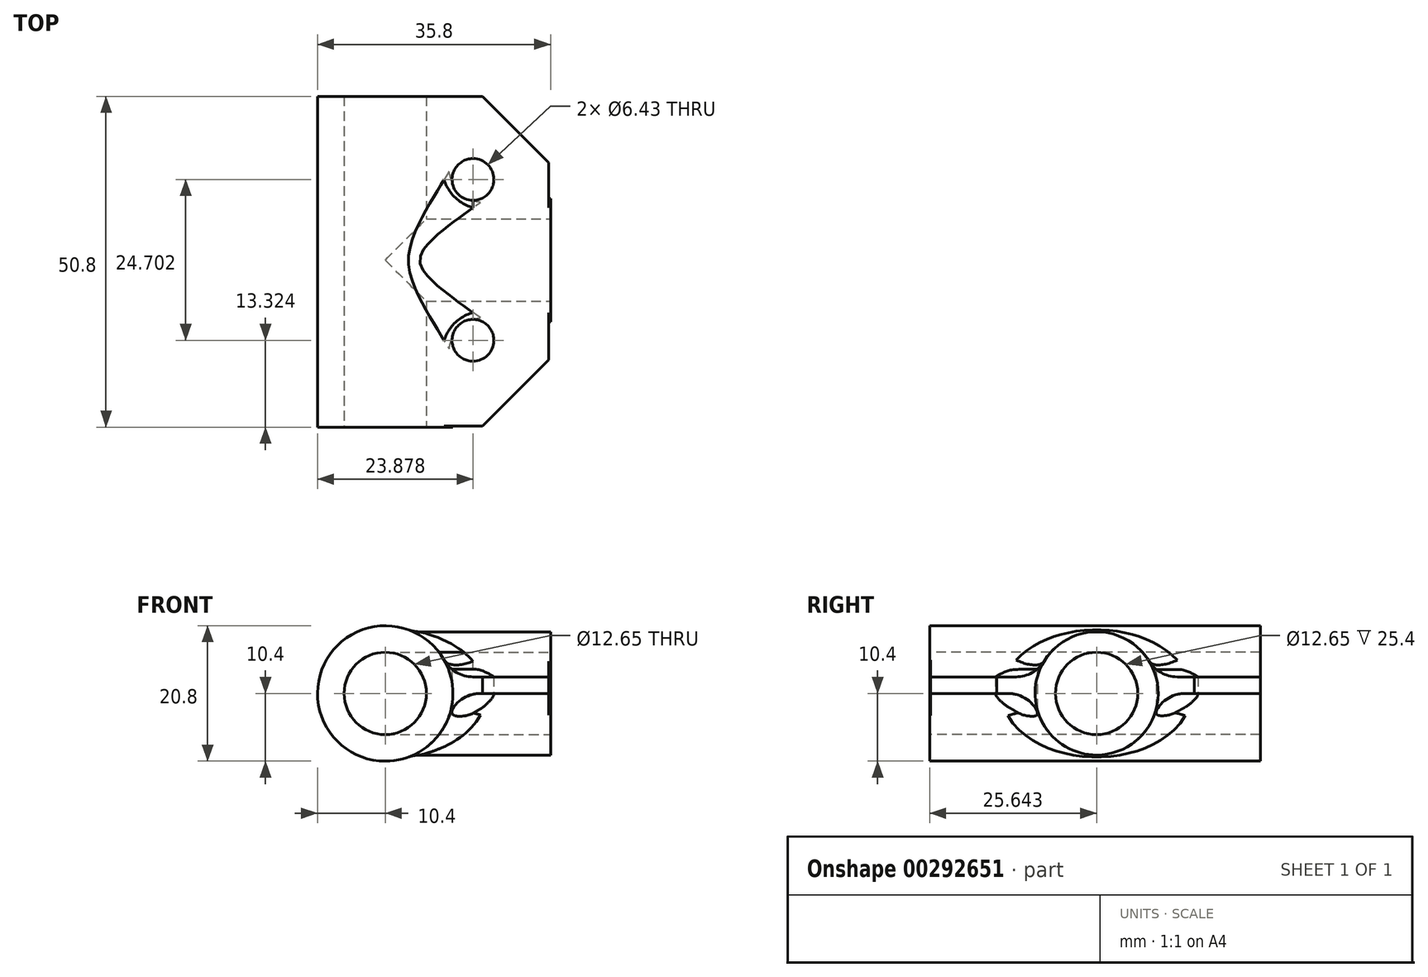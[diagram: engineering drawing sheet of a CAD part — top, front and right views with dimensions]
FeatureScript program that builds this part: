
annotation { "Feature Type Name" : "Feature", "Feature Type Description" : "" }
export const myFeature = defineFeature(function(context is Context, id is Id, definition is map)
    precondition{}
    {
        {
            var Q0;
            Q0=qCreatedBy(makeId("Front.planeOp"),FACE);
            var sketch = newSketch(context, id + "F0", { "sketchPlane" : qUnion([Q0])});
            skCircle(sketch, "E0", {"center": v(0, 0) * mm, "radius": 10.4 * mm});
            skSolve(sketch);
        }
        {
            var Q0;
            Q0=qCreatedBy(makeId("Top.planeOp"),FACE);
            var sketch = newSketch(context, id + "F1", { "sketchPlane" : qUnion([Q0])});
            skLineSegment(sketch, "E1.bottom", {"start": v(0, 0) * mm, "end": v(25.12, 0) * mm});
            skLineSegment(sketch, "E1.top", {"start": v(0, -50.67) * mm, "end": v(25.12, -50.67) * mm});
            skLineSegment(sketch, "E1.left", {"start": v(0, 0) * mm, "end": v(0, -50.67) * mm});
            skLineSegment(sketch, "E1.right", {"start": v(25.12, 0) * mm, "end": v(25.12, -50.67) * mm});
            skSolve(sketch);
        }
        {
            var Q0;
            Q0 = qSketchRegion(id + "F1", true);
            extrude(context, id + "F2", {"entities" : qUnion([Q0]), "depth" : 2.54 * mm});
        }
        {
            var Q0;
            Q0=makeQuery(id+"F0.imprint","IMPRINT",FACE,{"disambiguationData":[TD([[makeQuery(id+"F0.imprint","IMPRINT",EDGE,{"derivedFrom":sQuery(id+"F0.wireOp",EDGE,"E0")}),1.0]])]});
            var Q1;
            Q1=sQuery(id+"F0.wireOp",EDGE,"E0");
            extrude(context, id + "F3", {"entities" : qUnion([Q0]), "operationType" : NewBodyOperationType.ADD, "surfaceEntities" : qUnion([Q1]), "depth" : 50.8 * mm});
        }
        {
            var Q0;
            Q0=qCreatedBy(makeId("Right.planeOp"),FACE);
            var sketch = newSketch(context, id + "F4", { "sketchPlane" : qUnion([Q0])});
            skCircle(sketch, "E2", {"center": v(-25.16, 0) * mm, "radius": 9.46 * mm});
            skSolve(sketch);
        }
        {
            var Q0;
            Q0 = qSketchRegion(id + "F4", true);
            extrude(context, id + "F5", {"entities" : qUnion([Q0]), "operationType" : NewBodyOperationType.ADD, "depth" : 25.4 * mm});
        }
        {
            var Q0;
            {var subQ0=sQuery(id+"F1.wireOp",EDGE,"E1.top");var subQ1=makeQuery(id+"F2.opExtrude","CAP_FACE",FACE,{"disambiguationData":[OSD([sQuery(id+"F1.wireOp",EDGE,"E1.bottom"),subQ0,sQuery(id+"F1.wireOp",EDGE,"E1.left"),sQuery(id+"F1.wireOp",EDGE,"E1.right")])],"isStart":false});var subQ2=makeQuery(id+"F3.opExtrude","SWEPT_FACE",FACE,{"disambiguationData":[OSD([sQuery(id+"F0.wireOp",EDGE,"E0")])]});Q0=makeQuery(id+"F5.boolean.opBoolean","SPLIT",EDGE,{"disambiguationData":[TD([makeQuery(id+"F2.opExtrude","SWEPT_FACE",FACE,{"disambiguationData":[OSD([subQ0])]})])],"derivedFrom":makeQuery(id+"F3.boolean.opBoolean","INTERSECT",EDGE,{"derivedFrom":[subQ1,subQ2]})});}
            var Q1;
            Q1=makeQuery(id+"F5.boolean.opBoolean","INTERSECT",EDGE,{"disambiguationData":[OD(1.0)],"derivedFrom":[makeQuery(id+"F2.opExtrude","CAP_FACE",FACE,{"disambiguationData":[OSD([sQuery(id+"F1.wireOp",EDGE,"E1.bottom"),sQuery(id+"F1.wireOp",EDGE,"E1.top"),sQuery(id+"F1.wireOp",EDGE,"E1.left"),sQuery(id+"F1.wireOp",EDGE,"E1.right")])],"isStart":false}),makeQuery(id+"F5.opExtrude","SWEPT_FACE",FACE,{"disambiguationData":[OSD([sQuery(id+"F4.wireOp",EDGE,"E2")])]})]});
            fillet(context, id + "F6", {"entities" : qUnion([Q0, Q1]), "radius" : 5.08 * mm, "tangentPropagation" : true, "allowEdgeOverflow" : false});
        }
        {
            var Q0;
            Q0=makeQuery(id+"F5.boolean.opBoolean","INTERSECT",EDGE,{"disambiguationData":[OD(0.0)],"derivedFrom":[makeQuery(id+"F2.opExtrude","CAP_FACE",FACE,{"disambiguationData":[OSD([sQuery(id+"F1.wireOp",EDGE,"E1.bottom"),sQuery(id+"F1.wireOp",EDGE,"E1.top"),sQuery(id+"F1.wireOp",EDGE,"E1.left"),sQuery(id+"F1.wireOp",EDGE,"E1.right")])],"isStart":false}),makeQuery(id+"F5.opExtrude","SWEPT_FACE",FACE,{"disambiguationData":[OSD([sQuery(id+"F4.wireOp",EDGE,"E2")])]})]});
            fillet(context, id + "F7", {"entities" : qUnion([Q0]), "radius" : 5.08 * mm, "tangentPropagation" : true, "allowEdgeOverflow" : false});
        }
        {
            var Q0;
            {var subQ0=sQuery(id+"F0.wireOp",EDGE,"E0");var subQ1=makeQuery(id+"F3.opExtrude","SWEPT_FACE",FACE,{"disambiguationData":[OSD([subQ0])]});var subQ2=sQuery(id+"F1.wireOp",EDGE,"E1.bottom");var subQ3=makeQuery(id+"F2.opExtrude","CAP_FACE",FACE,{"disambiguationData":[OSD([subQ2,sQuery(id+"F1.wireOp",EDGE,"E1.top"),sQuery(id+"F1.wireOp",EDGE,"E1.left"),sQuery(id+"F1.wireOp",EDGE,"E1.right")])],"isStart":false});Q0=makeQuery(id+"F5.boolean.opBoolean","SPLIT",EDGE,{"disambiguationData":[TD([makeQuery(id+"F2.opExtrude","SWEPT_FACE",FACE,{"disambiguationData":[OSD([subQ2])]})])],"derivedFrom":makeQuery(id+"F3.boolean.opBoolean","INTERSECT",EDGE,{"derivedFrom":[subQ3,subQ1]})});}
            fillet(context, id + "F8", {"entities" : qUnion([Q0]), "radius" : 5.08 * mm, "tangentPropagation" : true, "allowEdgeOverflow" : false});
        }
        {
            var Q0;
            {var subQ0=sQuery(id+"F0.wireOp",EDGE,"E0");var subQ1=makeQuery(id+"F3.opExtrude","SWEPT_FACE",FACE,{"disambiguationData":[OSD([subQ0])]});var subQ2=sQuery(id+"F1.wireOp",EDGE,"E1.bottom");var subQ3=makeQuery(id+"F2.opExtrude","CAP_FACE",FACE,{"disambiguationData":[OSD([subQ2,sQuery(id+"F1.wireOp",EDGE,"E1.top"),sQuery(id+"F1.wireOp",EDGE,"E1.left"),sQuery(id+"F1.wireOp",EDGE,"E1.right")])],"isStart":true});Q0=makeQuery(id+"F5.boolean.opBoolean","SPLIT",EDGE,{"disambiguationData":[TD([makeQuery(id+"F2.opExtrude","SWEPT_FACE",FACE,{"disambiguationData":[OSD([subQ2])]})])],"derivedFrom":makeQuery(id+"F3.boolean.opBoolean","INTERSECT",EDGE,{"derivedFrom":[subQ3,subQ1]})});}
            var Q1;
            Q1=makeQuery(id+"F5.boolean.opBoolean","INTERSECT",EDGE,{"disambiguationData":[OD(0.0)],"derivedFrom":[makeQuery(id+"F2.opExtrude","CAP_FACE",FACE,{"disambiguationData":[OSD([sQuery(id+"F1.wireOp",EDGE,"E1.bottom"),sQuery(id+"F1.wireOp",EDGE,"E1.top"),sQuery(id+"F1.wireOp",EDGE,"E1.left"),sQuery(id+"F1.wireOp",EDGE,"E1.right")])],"isStart":true}),makeQuery(id+"F5.opExtrude","SWEPT_FACE",FACE,{"disambiguationData":[OSD([sQuery(id+"F4.wireOp",EDGE,"E2")])]})]});
            fillet(context, id + "F9", {"entities" : qUnion([Q0, Q1]), "radius" : 5.08 * mm, "tangentPropagation" : true, "allowEdgeOverflow" : false});
        }
        {
            var Q0;
            Q0=makeQuery(id+"F5.boolean.opBoolean","INTERSECT",EDGE,{"disambiguationData":[OD(1.0)],"derivedFrom":[makeQuery(id+"F2.opExtrude","CAP_FACE",FACE,{"disambiguationData":[OSD([sQuery(id+"F1.wireOp",EDGE,"E1.bottom"),sQuery(id+"F1.wireOp",EDGE,"E1.top"),sQuery(id+"F1.wireOp",EDGE,"E1.left"),sQuery(id+"F1.wireOp",EDGE,"E1.right")])],"isStart":true}),makeQuery(id+"F5.opExtrude","SWEPT_FACE",FACE,{"disambiguationData":[OSD([sQuery(id+"F4.wireOp",EDGE,"E2")])]})]});
            var Q1;
            {var subQ0=sQuery(id+"F1.wireOp",EDGE,"E1.top");var subQ1=makeQuery(id+"F2.opExtrude","CAP_FACE",FACE,{"disambiguationData":[OSD([sQuery(id+"F1.wireOp",EDGE,"E1.bottom"),subQ0,sQuery(id+"F1.wireOp",EDGE,"E1.left"),sQuery(id+"F1.wireOp",EDGE,"E1.right")])],"isStart":true});var subQ2=makeQuery(id+"F3.opExtrude","SWEPT_FACE",FACE,{"disambiguationData":[OSD([sQuery(id+"F0.wireOp",EDGE,"E0")])]});Q1=makeQuery(id+"F5.boolean.opBoolean","SPLIT",EDGE,{"disambiguationData":[TD([makeQuery(id+"F2.opExtrude","SWEPT_FACE",FACE,{"disambiguationData":[OSD([subQ0])]})])],"derivedFrom":makeQuery(id+"F3.boolean.opBoolean","INTERSECT",EDGE,{"derivedFrom":[subQ1,subQ2]})});}
            var Q2;
            Q2=makeQuery(id+"F5.boolean.opBoolean","INTERSECT",EDGE,{"disambiguationData":[OD(0.0)],"derivedFrom":[makeQuery(id+"F3.opExtrude","SWEPT_FACE",FACE,{"disambiguationData":[OSD([sQuery(id+"F0.wireOp",EDGE,"E0")])]}),makeQuery(id+"F5.opExtrude","SWEPT_FACE",FACE,{"disambiguationData":[OSD([sQuery(id+"F4.wireOp",EDGE,"E2")])]})]});
            fillet(context, id + "F10", {"entities" : qUnion([Q0, Q1, Q2]), "radius" : 5.08 * mm, "tangentPropagation" : true, "allowEdgeOverflow" : false});
        }
        {
            var Q0;
            Q0=makeQuery(id+"F3.opExtrude","CAP_FACE",FACE,{"disambiguationData":[OSD([sQuery(id+"F0.wireOp",EDGE,"E0")])],"isStart":false});
            var sketch = newSketch(context, id + "F11", { "sketchPlane" : qUnion([Q0])});
            skPoint(sketch, "E3", {"position": v(0, 0) * mm});
            skSolve(sketch);
        }
        {
            var Q0;
            Q0=sQuery(id+"F11.wireOp",VERTEX,"E3");
            var Q1;
            Q1=makeQuery(id+"F2.opExtrude","SWEPT_BODY",BODY,{"disambiguationData":[OSD([sQuery(id+"F1.wireOp",EDGE,"E1.bottom"),sQuery(id+"F1.wireOp",EDGE,"E1.top"),sQuery(id+"F1.wireOp",EDGE,"E1.left"),sQuery(id+"F1.wireOp",EDGE,"E1.right")])]});
            hole(context, id + "F12", {"style" : HoleStyle.SIMPLE, "endStyle" : HoleEndStyle.THROUGH, "holeDiameter" : 12.65 * mm, "tappedDepth" : 12.7 * mm, "tapClearance" : 3, "locations" : qUnion([Q0]), "scope" : qUnion([Q1])});
        }
        {
            var Q0;
            Q0=makeQuery(id+"F5.opExtrude","CAP_FACE",FACE,{"disambiguationData":[OSD([sQuery(id+"F4.wireOp",EDGE,"E2")])],"isStart":false});
            var sketch = newSketch(context, id + "F13", { "sketchPlane" : qUnion([Q0])});
            skPoint(sketch, "E4", {"position": v(-25.16, 0) * mm});
            skSolve(sketch);
        }
        {
            var Q0;
            Q0=sQuery(id+"F13.wireOp",VERTEX,"E4");
            var Q1;
            Q1=makeQuery(id+"F2.opExtrude","SWEPT_BODY",BODY,{"disambiguationData":[OSD([sQuery(id+"F1.wireOp",EDGE,"E1.bottom"),sQuery(id+"F1.wireOp",EDGE,"E1.top"),sQuery(id+"F1.wireOp",EDGE,"E1.left"),sQuery(id+"F1.wireOp",EDGE,"E1.right")])]});
            hole(context, id + "F14", {"style" : HoleStyle.SIMPLE, "endStyle" : HoleEndStyle.BLIND, "holeDiameter" : 12.65 * mm, "holeDepth" : 25.4 * mm, "tappedDepth" : 12.7 * mm, "tapClearance" : 3, "locations" : qUnion([Q0]), "scope" : qUnion([Q1])});
        }
        {
            var Q0;
            Q0=makeQuery(id+"F2.opExtrude","SWEPT_EDGE",EDGE,{"disambiguationData":[OSD([sQuery(id+"F1.wireOp",EDGE,"E1.top"),sQuery(id+"F1.wireOp",EDGE,"E1.right")])]});
            var Q1;
            Q1=makeQuery(id+"F2.opExtrude","SWEPT_EDGE",EDGE,{"disambiguationData":[OSD([sQuery(id+"F1.wireOp",EDGE,"E1.bottom"),sQuery(id+"F1.wireOp",EDGE,"E1.right")])]});
            chamfer(context, id + "F15", {"entities" : qUnion([Q0, Q1]), "width" : 10.16 * mm, "tangentPropagation" : true});
        }
        {
            var Q0;
            {var subQ1=sQuery(id+"F1.wireOp",EDGE,"E1.right");var subQ2=sQuery(id+"F1.wireOp",EDGE,"E1.bottom");Q0=makeQuery(id+"F5.boolean.opBoolean","SPLIT",FACE,{"disambiguationData":[TD([makeQuery(id+"F2.opExtrude","SWEPT_FACE",FACE,{"disambiguationData":[OSD([subQ2])]})])],"derivedFrom":makeQuery(id+"F2.opExtrude","CAP_FACE",FACE,{"disambiguationData":[OSD([subQ2,sQuery(id+"F1.wireOp",EDGE,"E1.top"),sQuery(id+"F1.wireOp",EDGE,"E1.left"),subQ1])],"isStart":false})});}
            var sketch = newSketch(context, id + "F16", { "sketchPlane" : qUnion([Q0])});
            skPoint(sketch, "E5", {"position": v(13.48, -12.77) * mm});
            skPoint(sketch, "E6", {"position": v(13.48, -37.48) * mm});
            skSolve(sketch);
        }
        {
            var Q0;
            Q0=sQuery(id+"F16.wireOp",VERTEX,"E5");
            var Q1;
            Q1=sQuery(id+"F16.wireOp",VERTEX,"E6");
            var Q2;
            Q2=makeQuery(id+"F2.opExtrude","SWEPT_BODY",BODY,{"disambiguationData":[OSD([sQuery(id+"F1.wireOp",EDGE,"E1.bottom"),sQuery(id+"F1.wireOp",EDGE,"E1.top"),sQuery(id+"F1.wireOp",EDGE,"E1.left"),sQuery(id+"F1.wireOp",EDGE,"E1.right")])]});
            hole(context, id + "F17", {"style" : HoleStyle.SIMPLE, "endStyle" : HoleEndStyle.BLIND, "oppositeDirection" : true, "holeDiameter" : 6.43 * mm, "holeDepth" : 25.4 * mm, "tappedDepth" : 12.7 * mm, "tapClearance" : 3, "locations" : qUnion([Q0, Q1]), "scope" : qUnion([Q2])});
        }
        {
            var Q0;
            Q0=sQuery(id+"F16.wireOp",VERTEX,"E5");
            var Q1;
            Q1=sQuery(id+"F16.wireOp",VERTEX,"E6");
            var Q2;
            Q2=makeQuery(id+"F2.opExtrude","SWEPT_BODY",BODY,{"disambiguationData":[OSD([sQuery(id+"F1.wireOp",EDGE,"E1.bottom"),sQuery(id+"F1.wireOp",EDGE,"E1.top"),sQuery(id+"F1.wireOp",EDGE,"E1.left"),sQuery(id+"F1.wireOp",EDGE,"E1.right")])]});
            hole(context, id + "F18", {"style" : HoleStyle.SIMPLE, "endStyle" : HoleEndStyle.BLIND, "holeDiameter" : 6.43 * mm, "holeDepth" : 25.4 * mm, "tappedDepth" : 12.7 * mm, "tapClearance" : 3, "locations" : qUnion([Q0, Q1]), "scope" : qUnion([Q2])});
        }
    });
